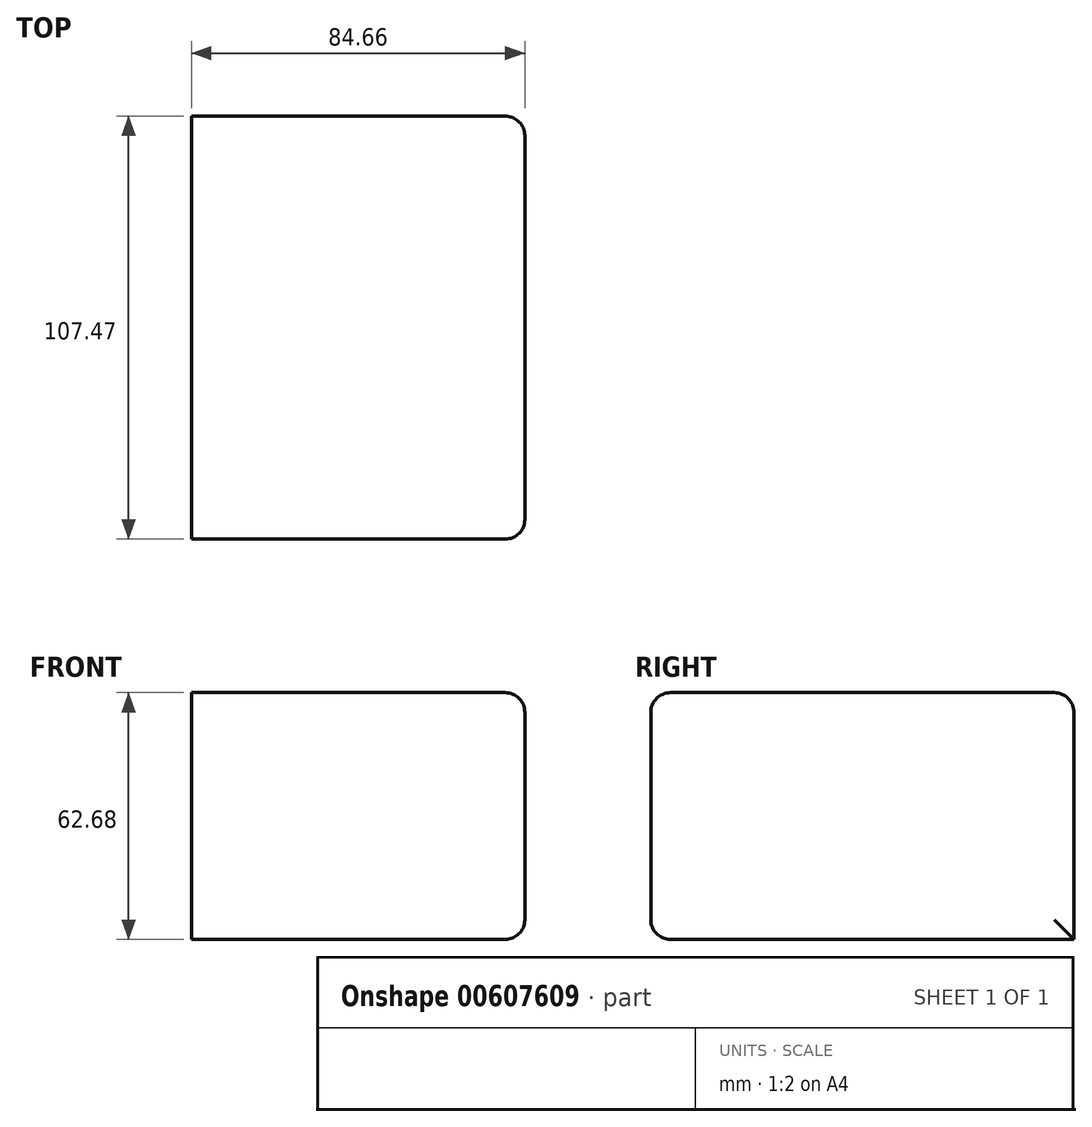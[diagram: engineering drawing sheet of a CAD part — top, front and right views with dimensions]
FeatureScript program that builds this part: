
annotation { "Feature Type Name" : "Feature", "Feature Type Description" : "" }
export const myFeature = defineFeature(function(context is Context, id is Id, definition is map)
    precondition{}
    {
        {
            var Q0;
            Q0=qCreatedBy(makeId("Front.planeOp"),FACE);
            var sketch = newSketch(context, id + "F0", { "sketchPlane" : qUnion([Q0])});
            skLineSegment(sketch, "E0.bottom", {"start": v(-51.68, 0) * mm, "end": v(32.98, 0) * mm});
            skLineSegment(sketch, "E0.top", {"start": v(-51.68, 62.68) * mm, "end": v(32.98, 62.68) * mm});
            skLineSegment(sketch, "E0.left", {"start": v(-51.68, 0) * mm, "end": v(-51.68, 62.68) * mm});
            skLineSegment(sketch, "E0.right", {"start": v(32.98, 0) * mm, "end": v(32.98, 62.68) * mm});
            skSolve(sketch);
        }
        {
            var Q0;
            Q0=makeQuery(id+"F0.imprint","IMPRINT",FACE,{"disambiguationData":[TD([[makeQuery(id+"F0.imprint","IMPRINT",EDGE,{"derivedFrom":sQuery(id+"F0.wireOp",EDGE,"E0.bottom")}),1.0]])]});
            var Q1;
            Q1 = qSketchRegion(id + "F0", true);
            extrude(context, id + "F1", {"entities" : qUnion([Q0, Q1]), "depth" : 107.47 * mm, "offsetDistance" : 25 * mm});
        }
        {
            var Q0;
            Q0=makeQuery(id+"F1.opExtrude","SWEPT_FACE",FACE,{"disambiguationData":[OSD([sQuery(id+"F0.wireOp",EDGE,"E0.right")])]});
            var Q1;
            Q1=makeQuery(id+"F1.opExtrude","CAP_EDGE",EDGE,{"disambiguationData":[OSD([sQuery(id+"F0.wireOp",EDGE,"E0.top")])],"isStart":false});
            var Q2;
            Q2=makeQuery(id+"F1.opExtrude","CAP_EDGE",EDGE,{"disambiguationData":[OSD([sQuery(id+"F0.wireOp",EDGE,"E0.top")])],"isStart":true});
            var Q3;
            Q3=makeQuery(id+"F1.opExtrude","CAP_EDGE",EDGE,{"disambiguationData":[OSD([sQuery(id+"F0.wireOp",EDGE,"E0.bottom")])],"isStart":false});
            fillet(context, id + "F2", {"entities" : qUnion([Q0, Q1, Q2, Q3]), "radius" : 5 * mm, "tangentPropagation" : true, "allowEdgeOverflow" : false});
        }
    });
